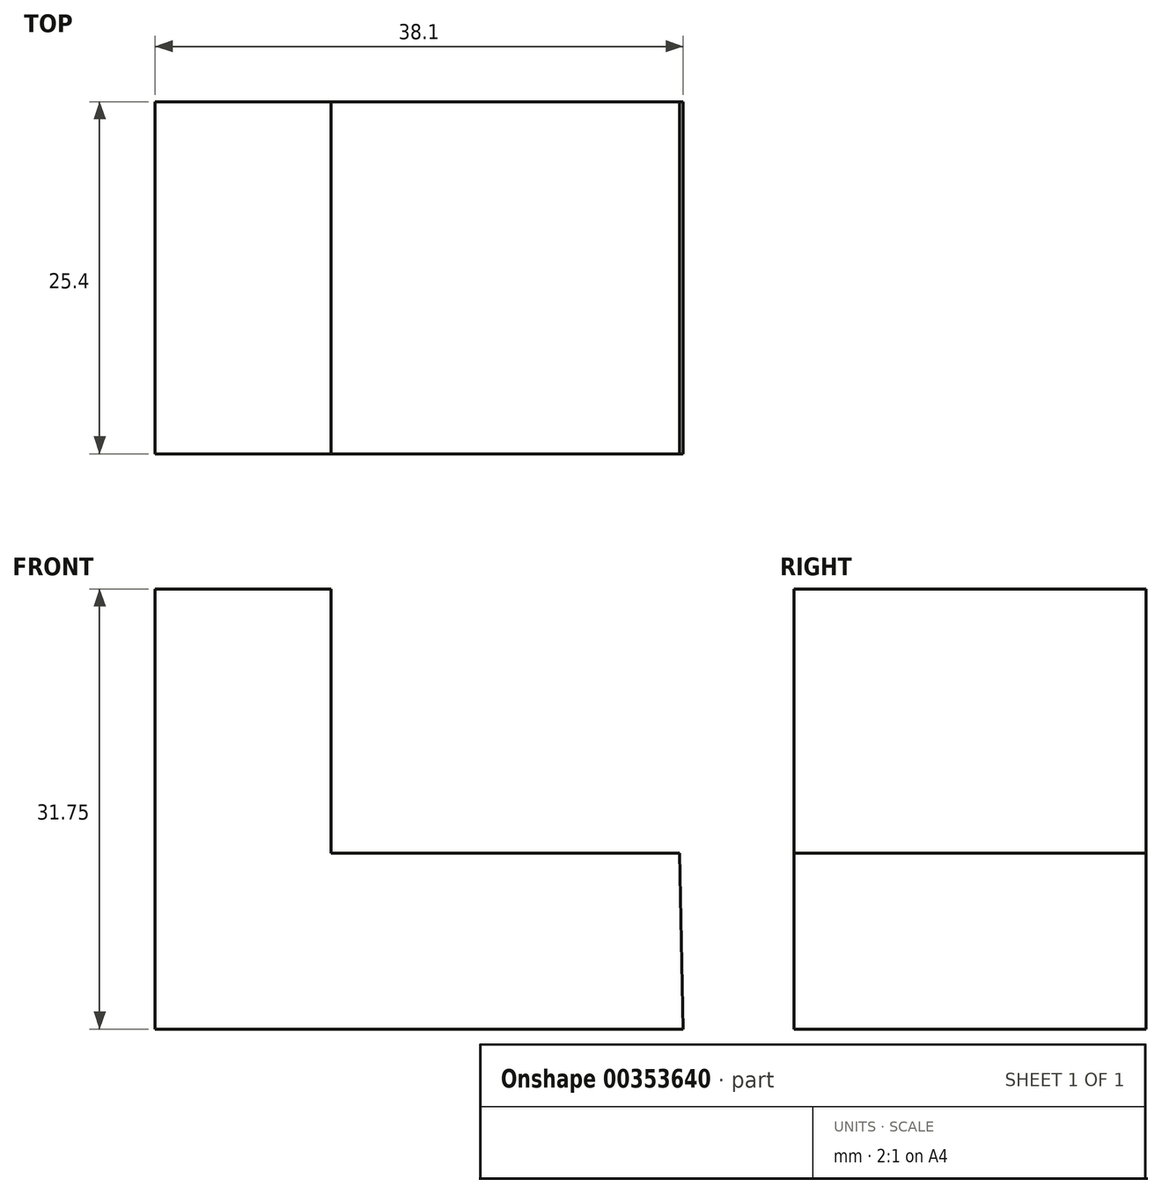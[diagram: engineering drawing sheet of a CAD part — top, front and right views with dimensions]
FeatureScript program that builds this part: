
annotation { "Feature Type Name" : "Feature", "Feature Type Description" : "" }
export const myFeature = defineFeature(function(context is Context, id is Id, definition is map)
    precondition{}
    {
        {
            var Q0;
            Q0=qCreatedBy(makeId("Front.planeOp"),FACE);
            var sketch = newSketch(context, id + "F0", { "sketchPlane" : qUnion([Q0])});
            skLineSegment(sketch, "E0", {"start": v(0, 0) * mm, "end": v(0, 31.75) * mm});
            skLineSegment(sketch, "E1", {"start": v(0, 0) * mm, "end": v(38.1, 0) * mm});
            skLineSegment(sketch, "E2", {"start": v(0, 31.75) * mm, "end": v(12.7, 31.75) * mm});
            skLineSegment(sketch, "E3", {"start": v(12.7, 31.75) * mm, "end": v(12.7, 12.7) * mm});
            skLineSegment(sketch, "E4", {"start": v(12.7, 12.7) * mm, "end": v(37.83, 12.7) * mm});
            skLineSegment(sketch, "E5", {"start": v(37.83, 12.7) * mm, "end": v(38.1, 0) * mm});
            skSolve(sketch);
        }
        {
            var Q0;
            Q0=makeQuery(id+"F0.imprint","IMPRINT",FACE,{"disambiguationData":[TD([[makeQuery(id+"F0.imprint","IMPRINT",EDGE,{"derivedFrom":sQuery(id+"F0.wireOp",EDGE,"E0")}),-1.0]])]});
            extrude(context, id + "F1", {"entities" : qUnion([Q0]), "depth" : 25.4 * mm});
        }
    });
